FCSTD DOCUMENT  (FreeCAD 0.16R6707 (Git))
Label: Pata
License: All rights reserved
LicenseURL: http://en.wikipedia.org/wiki/All_rights_reserved
objects: Sketcher::SketchObject×1
note: 1 computed .brp shape members not serialized (recipe doc carries the construction recipe); baked Part::Feature solids carry a one-line shape summary decoded from their .brp

FEATURE [Sketcher::SketchObject] Sketch
  sketch-geometry (7):
    g0: LineSegment StartX=0 StartY=20 StartZ=0 EndX=0 EndY=0 EndZ=0
    g1: LineSegment StartX=0 StartY=0 StartZ=0 EndX=13 EndY=0 EndZ=0
    g2: LineSegment StartX=13 StartY=0 StartZ=0 EndX=13 EndY=20 EndZ=0
    g3: LineSegment StartX=2 StartY=20 StartZ=0 EndX=2 EndY=7 EndZ=0
    g4: LineSegment StartX=11 StartY=20 StartZ=0 EndX=11 EndY=7 EndZ=0
    g5: LineSegment StartX=0 StartY=20 StartZ=0 EndX=2 EndY=20 EndZ=0
    g6: LineSegment StartX=13 StartY=20 StartZ=0 EndX=11 EndY=20 EndZ=0
  constraints (21):
    c: Vertical(g0)
    c: Horizontal(g1)
    c: Coincident(g2,g1)
    c: Vertical(g2)
    c: DistanceX(g1,g1) = 13
    c: Equal(g0,g2)
    c: DistanceY(g0,g0) = 20
    c: Coincident(g0,g-1)
    c: Coincident(g1,g-1)
    c: Vertical(g3)
    c: Vertical(g4)
    c: Coincident(g5,g0)
    c: Coincident(g5,g3)
    c: Coincident(g6,g2)
    c: Coincident(g6,g4)
    c: Horizontal(g6)
    c: Equal(g6,g5)
    c: Horizontal(g5)
    c: Equal(g4,g3)
    c: DistanceX(g6,g6) = 2
    c: DistanceY(g3,g3) = 13
